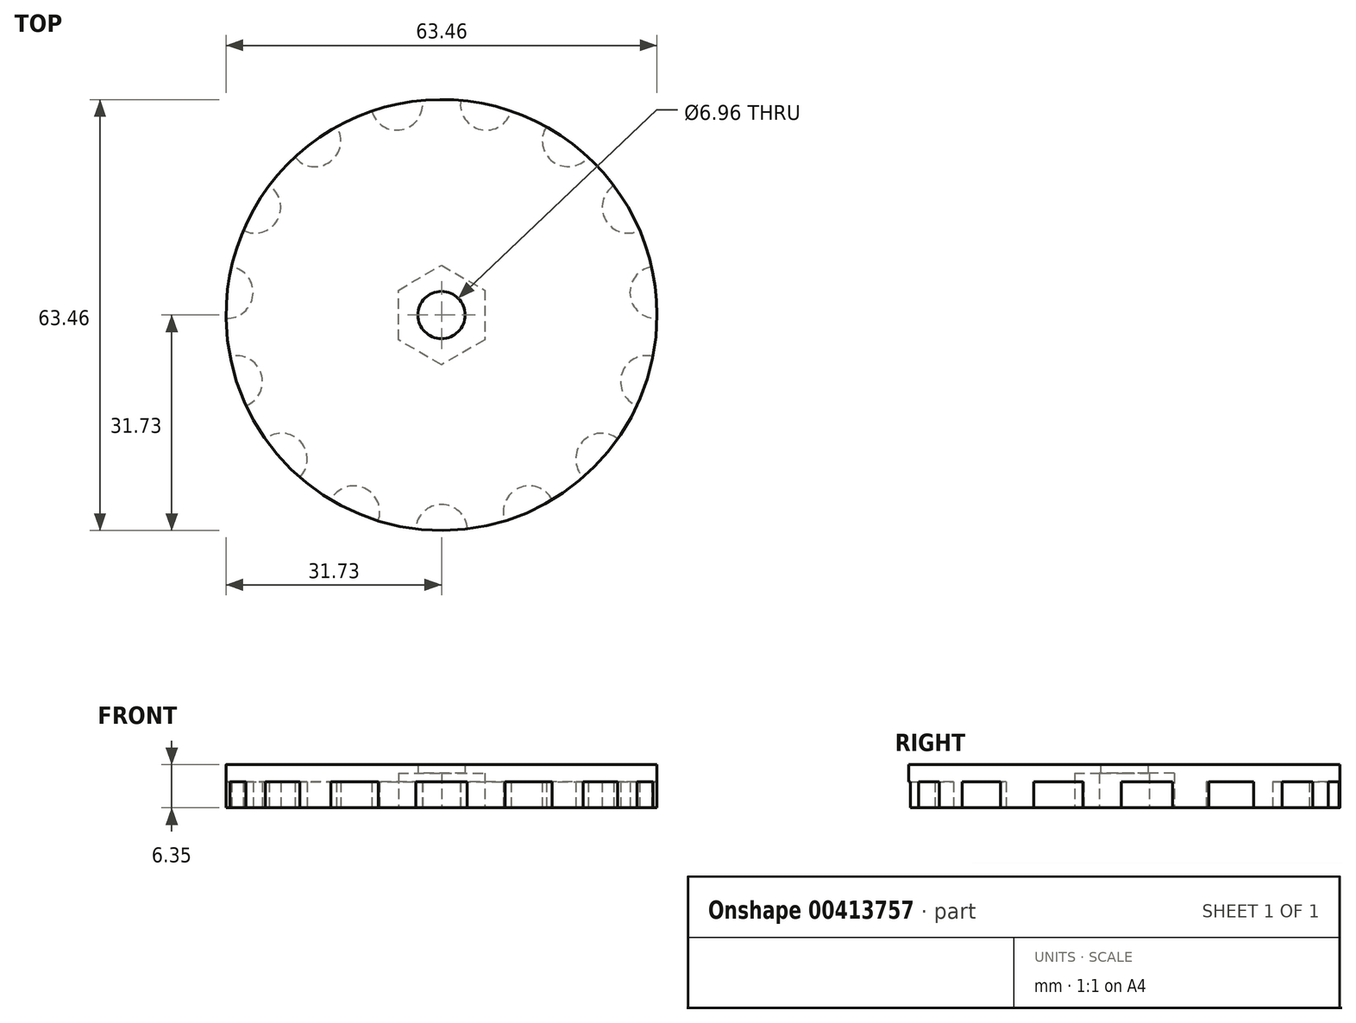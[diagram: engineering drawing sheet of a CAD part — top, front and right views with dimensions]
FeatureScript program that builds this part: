
annotation { "Feature Type Name" : "Feature", "Feature Type Description" : "" }
export const myFeature = defineFeature(function(context is Context, id is Id, definition is map)
    precondition{}
    {
        {
            var Q0;
            Q0=qCreatedBy(makeId("Top.planeOp"),FACE);
            var sketch = newSketch(context, id + "F0", { "sketchPlane" : qUnion([Q0])});
            skCircle(sketch, "E0", {"center": v(0, 0) * mm, "radius": 31.73 * mm});
            skCircle(sketch, "E1", {"center": v(0, 0) * mm, "radius": 3.48 * mm});
            skSolve(sketch);
        }
        {
            var Q0;
            Q0=makeQuery(id+"F0.imprint","IMPRINT",FACE,{"disambiguationData":[TD([[makeQuery(id+"F0.imprint","IMPRINT",EDGE,{"derivedFrom":sQuery(id+"F0.wireOp",EDGE,"E0")}),1.0]])]});
            extrude(context, id + "F1", {"entities" : qUnion([Q0]), "depth" : 6.35 * mm});
        }
        {
            var Q0;
            Q0=qCreatedBy(makeId("Top.planeOp"),FACE);
            var sketch = newSketch(context, id + "F2", { "sketchPlane" : qUnion([Q0])});
            skCircle(sketch, "E2.cCircle", {"center": v(0, 0) * mm, "radius": 6.35 * mm, "construction": true});
            skLineSegment(sketch, "E2.0", {"start": v(6.35, 3.67) * mm, "end": v(6.35, -3.67) * mm});
            skLineSegment(sketch, "E2.1", {"start": v(6.35, -3.67) * mm, "end": v(0, -7.33) * mm});
            skLineSegment(sketch, "E2.2", {"start": v(0, -7.33) * mm, "end": v(-6.35, -3.67) * mm});
            skLineSegment(sketch, "E2.3", {"start": v(-6.35, -3.67) * mm, "end": v(-6.35, 3.67) * mm});
            skLineSegment(sketch, "E2.4", {"start": v(-6.35, 3.67) * mm, "end": v(0, 7.33) * mm});
            skLineSegment(sketch, "E2.5", {"start": v(0, 7.33) * mm, "end": v(6.35, 3.67) * mm});
            skPoint(sketch, "E2.0.midPoint", {"position": v(6.35, 0) * mm});
            skSolve(sketch);
        }
        {
            var Q0;
            Q0=makeQuery(id+"F2.imprint","IMPRINT",FACE,{"disambiguationData":[TD([[makeQuery(id+"F2.imprint","IMPRINT",EDGE,{"derivedFrom":sQuery(id+"F2.wireOp",EDGE,"E2.0")}),-1.0]])]});
            extrude(context, id + "F3", {"entities" : qUnion([Q0]), "operationType" : NewBodyOperationType.REMOVE, "depth" : 5.08 * mm});
        }
        {
            var Q0;
            Q0=qCreatedBy(makeId("Top.planeOp"),FACE);
            var sketch = newSketch(context, id + "F4", { "sketchPlane" : qUnion([Q0])});
            skCircle(sketch, "E3.0", {"center": v(0, 0) * mm, "radius": 31.73 * mm, "construction": true});
            skCircle(sketch, "E4", {"center": v(0, -31.73) * mm, "radius": 3.81 * mm});
            skCircle(sketch, "E5.1.0", {"center": v(12.9, -28.99) * mm, "radius": 3.81 * mm});
            skCircle(sketch, "E5.2.0", {"center": v(23.58, -21.23) * mm, "radius": 3.8 * mm});
            skCircle(sketch, "E5.3.0", {"center": v(30.18, -9.8) * mm, "radius": 3.81 * mm});
            skCircle(sketch, "E5.4.0", {"center": v(31.55, 3.32) * mm, "radius": 3.81 * mm});
            skCircle(sketch, "E5.5.0", {"center": v(27.48, 15.86) * mm, "radius": 3.81 * mm});
            skCircle(sketch, "E5.6.0", {"center": v(18.65, 25.67) * mm, "radius": 3.81 * mm});
            skCircle(sketch, "E5.7.0", {"center": v(6.6, 31.03) * mm, "radius": 3.81 * mm});
            skCircle(sketch, "E5.8.0", {"center": v(-6.6, 31.03) * mm, "radius": 3.81 * mm});
            skCircle(sketch, "E5.9.0", {"center": v(-18.65, 25.67) * mm, "radius": 3.81 * mm});
            skCircle(sketch, "E5.10.0", {"center": v(-27.48, 15.86) * mm, "radius": 3.81 * mm});
            skCircle(sketch, "E5.11.0", {"center": v(-31.55, 3.32) * mm, "radius": 3.81 * mm});
            skCircle(sketch, "E5.12.0", {"center": v(-30.18, -9.8) * mm, "radius": 3.81 * mm});
            skCircle(sketch, "E5.13.0", {"center": v(-23.58, -21.23) * mm, "radius": 3.81 * mm});
            skCircle(sketch, "E5.14.0", {"center": v(-12.9, -28.99) * mm, "radius": 3.81 * mm});
            skSolve(sketch);
        }
        {
            var Q0;
            Q0 = qSketchRegion(id + "F4", true);
            extrude(context, id + "F5", {"entities" : qUnion([Q0]), "operationType" : NewBodyOperationType.REMOVE, "depth" : 3.8 * mm});
        }
    });
